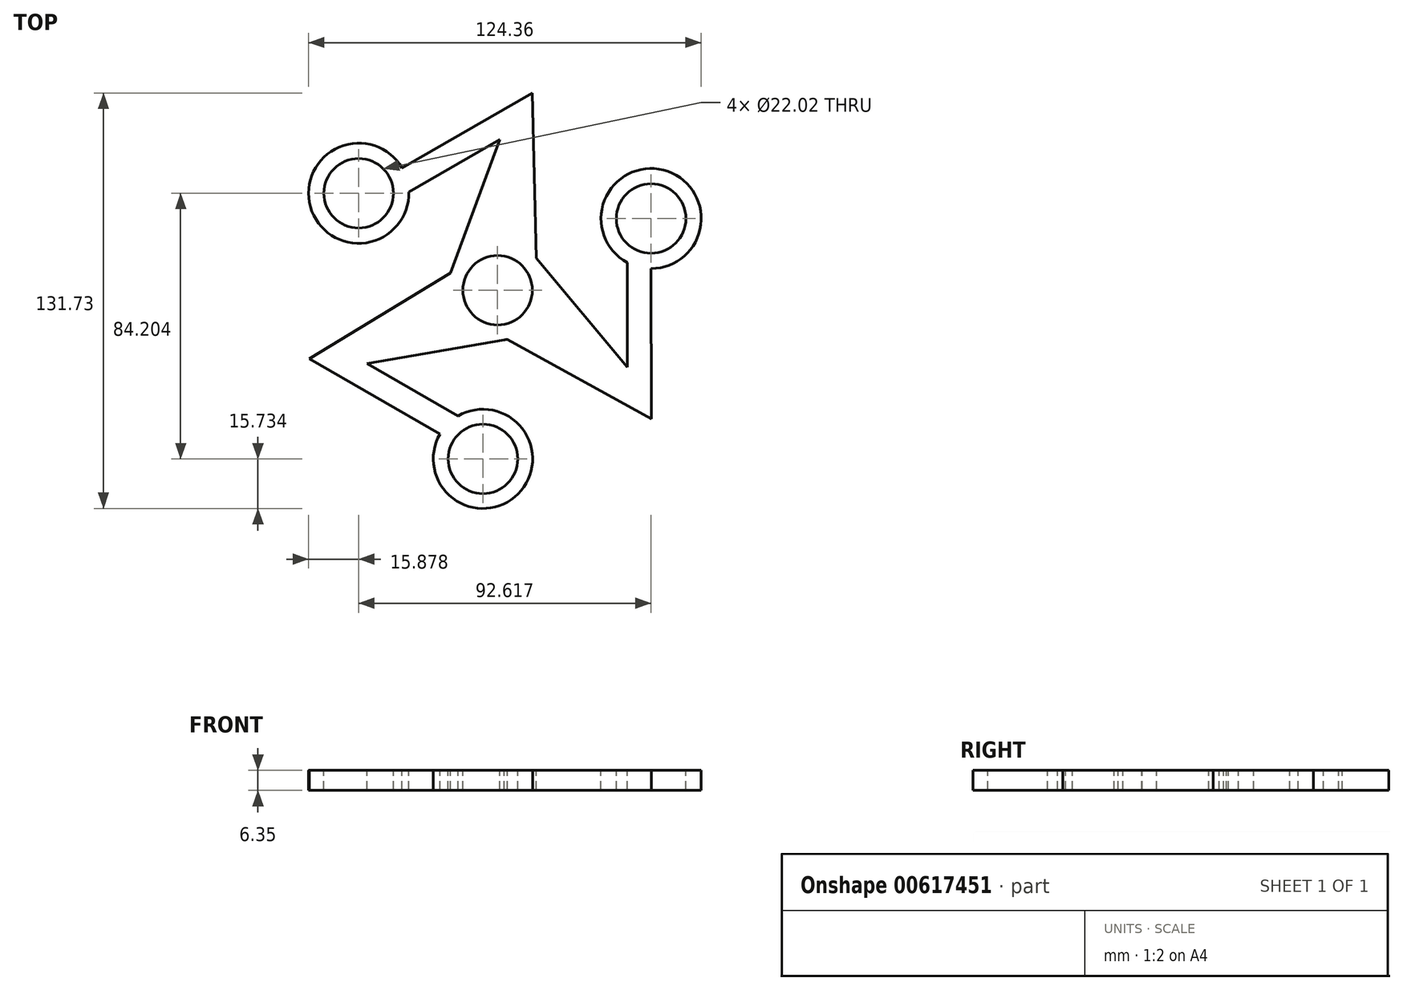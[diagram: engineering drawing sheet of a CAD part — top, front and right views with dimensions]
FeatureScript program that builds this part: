
annotation { "Feature Type Name" : "Feature", "Feature Type Description" : "" }
export const myFeature = defineFeature(function(context is Context, id is Id, definition is map)
    precondition{}
    {
        {
            var Q0;
            Q0=qCreatedBy(makeId("Top.planeOp"),FACE);
            var sketch = newSketch(context, id + "F0", { "sketchPlane" : qUnion([Q0])});
            skCircle(sketch, "E0", {"center": v(0, 0) * mm, "radius": 11.01 * mm});
            skLineSegment(sketch, "E1", {"start": v(10.97, 62.54) * mm, "end": v(-30.25, 38.7) * mm});
            skLineSegment(sketch, "E2", {"start": v(-59.66, -21.75) * mm, "end": v(-18.26, -45.6) * mm});
            skLineSegment(sketch, "E3", {"start": v(48.68, -40.78) * mm, "end": v(48.64, 6.86) * mm});
            skCircle(sketch, "E4", {"center": v(-44, 30.75) * mm, "radius": 11.01 * mm});
            skCircle(sketch, "E5", {"center": v(48.62, 22.72) * mm, "radius": 11.01 * mm});
            skCircle(sketch, "E6", {"center": v(-4.64, -53.46) * mm, "radius": 11.01 * mm});
            skArc(sketch, "E7", {"start": v(-30.25, 38.7) * mm, "mid": v(-59.27, 26.44) * mm, "end": v(-28.12, 31.15) * mm});
            skArc(sketch, "E8", {"start": v(48.64, 6.86) * mm, "mid": v(52.54, 38.1) * mm, "end": v(41.02, 8.8) * mm});
            skArc(sketch, "E9", {"start": v(-18.26, -45.6) * mm, "mid": v(6.5, -64.57) * mm, "end": v(-12.5, -39.84) * mm});
            skLineSegment(sketch, "E10.trimOffspring", {"start": v(0.64, 47.8) * mm, "end": v(-28.12, 31.15) * mm});
            skLineSegment(sketch, "E11", {"start": v(0.64, 47.8) * mm, "end": v(-14.9, 5.5) * mm});
            skLineSegment(sketch, "E12.trimOffspring", {"start": v(41.05, -24.43) * mm, "end": v(41.02, 8.8) * mm});
            skLineSegment(sketch, "E13", {"start": v(41.05, -24.43) * mm, "end": v(12.2, 10.17) * mm});
            skLineSegment(sketch, "E14.trimOffspring", {"start": v(-41.3, -23.24) * mm, "end": v(-12.5, -39.84) * mm});
            skLineSegment(sketch, "E15", {"start": v(-41.3, -23.24) * mm, "end": v(3.1, -15.56) * mm});
            skLineSegment(sketch, "E16", {"start": v(-14.9, 5.5) * mm, "end": v(-59.66, -21.75) * mm});
            skLineSegment(sketch, "E17", {"start": v(3.1, -15.56) * mm, "end": v(48.68, -40.78) * mm});
            skLineSegment(sketch, "E18", {"start": v(12.2, 10.17) * mm, "end": v(10.97, 62.54) * mm});
            skCircle(sketch, "E19", {"center": v(0, 0) * mm, "radius": 15.88 * mm});
            skSolve(sketch);
        }
        {
            var Q0;
            Q0=makeQuery(id+"F0.imprint","IMPRINT",FACE,{"disambiguationData":[TD([[makeQuery(id+"F0.imprint","IMPRINT",EDGE,{"derivedFrom":sQuery(id+"F0.wireOp",EDGE,"E0")}),-1.0]])]});
            var Q1;
            Q1=makeQuery(id+"F0.imprint","IMPRINT",FACE,{"disambiguationData":[TD([[makeQuery(id+"F0.imprint","IMPRINT",EDGE,{"derivedFrom":sQuery(id+"F0.wireOp",EDGE,"E1")}),1.0]])]});
            var Q2;
            {var subQ0=sQuery(id+"F0.wireOp",EDGE,"E17");var subQ1=sQuery(id+"F0.wireOp",EDGE,"E15");var subQ2=makeQuery(id+"F0.imprint","INTERSECT",VERTEX,{"derivedFrom":[subQ1,subQ0]});Q2=makeQuery(id+"F0.imprint","IMPRINT",FACE,{"disambiguationData":[TD([[makeQuery(id+"F0.imprint","IMPRINT",EDGE,{"disambiguationData":[TD([[subQ2,1.0]])],"derivedFrom":subQ1}),-1.0]])]});}
            extrude(context, id + "F1", {"entities" : qUnion([Q0, Q1, Q2]), "oppositeDirection" : true, "depth" : 6.35 * mm, "offsetDistance" : 25.4 * mm});
        }
    });
